# Revit family: AD-C.SUB
name_source: partatom
category: Communication Devices
revit_build: Autodesk Revit 2015 (Build: 20160512_0715(x64)
units: mm (PartAtom-declared; Revit-internal decimal feet)

## types (1)
- AD-C.SUB
    100V Taps = 25, 50, 100
    70V Taps = 12.5, 25, 50, 100
    Coverage Horizontal = 360.00°
    Coverage Vertical = 360.00°
    Default Elevation = 0 mm
    Depth = 254 mm
    Description = 6.5 inch dual voice-coil, small format ceiling subwoofer
    Dim1 = 150 mm
    Impedance = 4
    Manufacturer = QSC
    Manufacturer URL = www.qsc.com
    Model = AD-C.SUB
    Product Documentation Link = https://www.qsc.com
    Product Page URL = https://www.qsc.com
    Regulatory Compliance = UL1480, UL2043, NFPA90, NFPA70 suitable for use in air handling spaces. Transformer UL registered per UL1876, ROHS, CE compliant. 
Baffle meets UL94-V0 and UL94-5VB flamibility rating; in accordance with IEC60849 / EN60849 systems
    SPL Max = 106
    Sensitivity = 86
    URL = https://www.qsc.com
    Weight Product (kg) = 8.7
    Weight Product (lb) = 19.2
    White plastic = White Powder Coated Finish
    Width = 340 mm
    dim2 = 17 mm
    dim3 = 150 mm
    dim4 = 170 mm
    dim5 = 5 mm
    dim6 = 144 mm
    dim7 = 155 mm

## geometry (parser evidence)
native form markers: Blend x6, Sweep x2
no freeform markers — native parametric forms only
